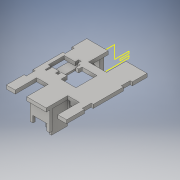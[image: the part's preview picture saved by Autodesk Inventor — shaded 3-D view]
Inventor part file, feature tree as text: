
AUTODESK INVENTOR PART (.ipt)
format: ipt  version: 2016 (Build 200138000, 138)  size: 601,088 bytes
history: native  units: in
note: dims shown in document units (in); Inventor stores cm internally (conversion verified against a paired STEP export)
features: reference x41, extrude x31, sketch x31, plane x6, projected_geometry x3
ambient origin geometry x8: Origin, YZ Plane, XZ Plane, XY Plane, X Axis, Y Axis, Z Axis, Center Point
bodies: Solid1 (feature_tree)
feature tree (112):
  extrude  "Extrusion1"  Depth=3.0in
  extrude  "Extrusion2"  Depth=0.0787in
  extrude  "Extrusion3"  Depth=1.0827in
  extrude  "Extrusion5"  Depth=1.0in TaperAngle=0.0deg
  plane  "Work Plane1"
  extrude  "Extrusion6"  Depth=0.0098in
  extrude  "Extrusion14"  Depth=0.0787in
  plane  "Work Plane2"
  extrude  "Extrusion16"  Depth=0.1575in
  extrude  "Extrusion17"  Depth=1.25in
  extrude  "Extrusion18"  Depth=0.1575in
  plane  "Work Plane3"
  extrude  "Extrusion20"  Depth=0.1969in
  extrude  "Extrusion21"  Depth=0.1969in
  plane  "Work Plane4"
  plane  "Work Plane5"
  extrude  "Extrusion23"  Depth=0.1181in TaperAngle=0.0deg
  extrude  "Extrusion24"  Depth=0.1181in
  plane  "Work Plane6"
  extrude  "Extrusion25"  Depth=0.1969in TaperAngle=0.0deg
  extrude  "Extrusion26"  Depth=0.35in
  extrude  "Extrusion27"  Depth=0.2in
  extrude  "Extrusion28"  Depth=0.1969in TaperAngle=0.0deg
  extrude  "Extrusion29"  Depth=1.5in
  extrude  "Extrusion30"  Depth=0.1181in
  extrude  "Extrusion31"  Depth=0.1181in TaperAngle=0.0deg
  extrude  "Extrusion34"  Depth=1.0in
  sketch  "Sketch36"  dims[d98=0.1181in d99=0.0in d104=1.0in]
  extrude  "Extrusion35"  Depth=0.5in
  extrude  "Extrusion36"  Depth=0.5in
  extrude  "Extrusion37"  Depth=0.0197in
  extrude  "Extrusion38"  Depth=0.325in
  extrude  "Extrusion39"  Depth=0.1969in
  sketch  "Sketch41"  dims[d114=0.197in d115=0.0in d116=0.1969in]
  extrude  "Extrusion40"  Depth=0.1181in
  extrude  "Extrusion41"  Depth=0.1575in TaperAngle=0.0deg
  extrude  "Extrusion42"  Depth=1.0in TaperAngle=0.0deg
  extrude  "Extrusion43"  Depth=0.5in
  extrude  "Extrusion44"  Depth=0.9in
  sketch  "Sketch1"  dims[d0=4.5in d1=3.0in]
  sketch  "Sketch2"  dims[d2=0.1969in d3=0.0in d5=0.0787in]
  reference  "Reference1"
  reference  "Reference2"
  sketch  "Sketch3"  dims[d6=1.0in d7=0.0in d8=1.0827in]
  sketch  "Sketch5"  dims[d9=0.3937in d10=1.0in d11=0.0in]
  reference  "Reference14"
  reference  "Reference15"
  reference  "Reference16"
  reference  "Reference17"
  reference  "Reference18"
  sketch  "Sketch6"  dims[d12=0.0787in d23=0.0098in]
  reference  "Reference19"
  sketch  "Sketch14"  dims[d24=0.1575in d25=0.0787in]
  sketch  "Sketch16"  dims[d26=0.0098in d27=0.1575in]
  reference  "Reference30"
  sketch  "Sketch17"  dims[d28=0.1181in d29=0.0in d30=1.25in]
  reference  "Reference31"
  reference  "Reference32"
  reference  "Reference33"
  reference  "Reference35"
  reference  "Reference36"
  reference  "Reference37"
  reference  "Reference38"
  reference  "Reference39"
  reference  "Reference40"
  reference  "Reference41"
  reference  "Reference42"
  reference  "Reference43"
  reference  "Reference44"
  reference  "Reference45"
  reference  "Reference46"
  reference  "Reference47"
  reference  "Reference48"
  reference  "Reference49"
  sketch  "Sketch20"  dims[d31=0.1575in d32=0.1575in]
  reference  "Reference50"
  sketch  "Sketch21"  dims[d33=0.1181in d34=0.0in d58=0.1969in]
  sketch  "Sketch23"  dims[d59=0.1969in d60=0.1969in]
  reference  "Reference53"
  reference  "Reference54"
  sketch  "Sketch24"  dims[d61=0.1969in d62=0.0in d65=0.1181in d66=0.0in]
  sketch  "Sketch25"  dims[d67=0.1969in d68=0.0in d69=0.1181in]
  reference  "Reference55"
  reference  "Reference56"
  sketch  "Sketch26"  dims[d70=0.1181in d71=0.1969in d72=0.0in]
  reference  "Reference57"
  reference  "Reference58"
  sketch  "Sketch28"  dims[d75=0.0394in d76=0.35in]
  sketch  "Sketch29"  dims[d77=0.1628in d78=0.2in]
  sketch  "Sketch30"  dims[d79=0.0787in d80=0.0in d81=0.1969in d82=0.0in]
  reference  "Reference59"
  sketch  "Sketch31"  dims[d89=1.5in d90=1.5in]
  sketch  "Sketch32"  dims[d91=0.1181in d92=0.0in d93=0.7in]
  sketch  "Sketch35"  dims[d94=1.26in d95=0.0in d96=0.1181in d97=0.0in]
  reference  "Reference61"
  sketch  "Sketch37"  dims[d105=0.1181in d106=0.5in]
  reference  "Reference62"
  sketch  "Sketch38"  dims[d107=1.0in d108=0.5in]
  reference  "Reference63"
  sketch  "Sketch39"  dims[d109=10.0in d110=0.0in d111=0.0197in]
  reference  "Reference64"
  sketch  "Sketch40"  dims[d112=0.0197in d113=0.325in]
  reference  "Reference65"
  projected_geometry  "Projected Loop6"
  sketch  "Sketch42"  dims[d117=0.1969in d118=0.1181in]
  projected_geometry  "Projected Loop7"
  sketch  "Sketch43"  dims[d119=0.1969in d120=0.0in d121=0.1575in d122=0.0in]
  reference  "Reference66"
  sketch  "Sketch44"  dims[d123=0.1in d124=0.0in d132=1.0in d133=0.0in]
  projected_geometry  "Projected Loop8"
  sketch  "Sketch45"  dims[d134=0.5in d135=0.5in]
  sketch  "Sketch46"  dims[d136=0.0039in d137=0.0039in d138=0.0984in d139=0.0984in d140=0.0039in d141=0.0984in d142=1.61in d143=0.0in d144=0.2in d145=0.0in d146=0.2362in d147=0.85in d148=0.0in d149=1.2in d150=0.2362in d151=1.1in d152=0.0in d153=0.325in d154=3.0in d155=0.0in d156=989.0in d157=0.0in d158=0.0098in d159=0.0098in d160=0.0098in d161=1.0in d162=0.0in d163=0.2784in d164=0.0in d165=0.15in d166=1323.0in d167=0.0in d168=0.0787in d169=0.0787in d170=0.9in d171=0.0in d172=0.2579in d173=0.3in]
